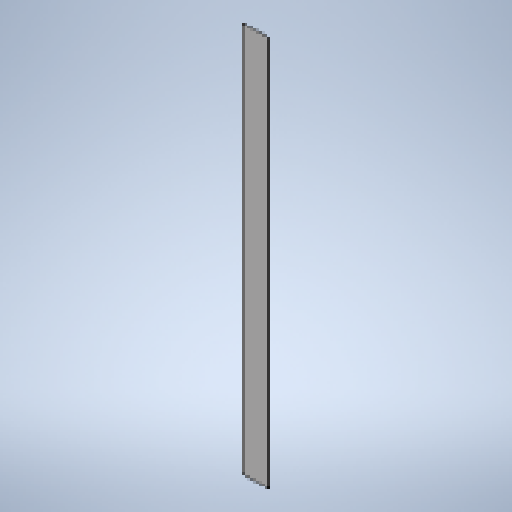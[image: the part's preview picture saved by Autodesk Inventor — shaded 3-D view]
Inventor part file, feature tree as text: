
AUTODESK INVENTOR PART (.ipt)
format: ipt  version: 2025 (Build 290162010, 162A)  size: 142,848 bytes
history: native  units: mm
features: sheet_metal_op x1, sketch x1, other x1
ambient origin geometry x8: Origin, YZ Plane, XZ Plane, XY Plane, X Axis, Y Axis, Z Axis, Center Point
bodies: Solid1 (feature_tree)
feature tree (3):
  sheet_metal_op  "Face1"
  sketch  "Sketch1"  dims[d0=200.0mm d1=2920.0mm d2=2.0mm]
  other  "Plate1"
